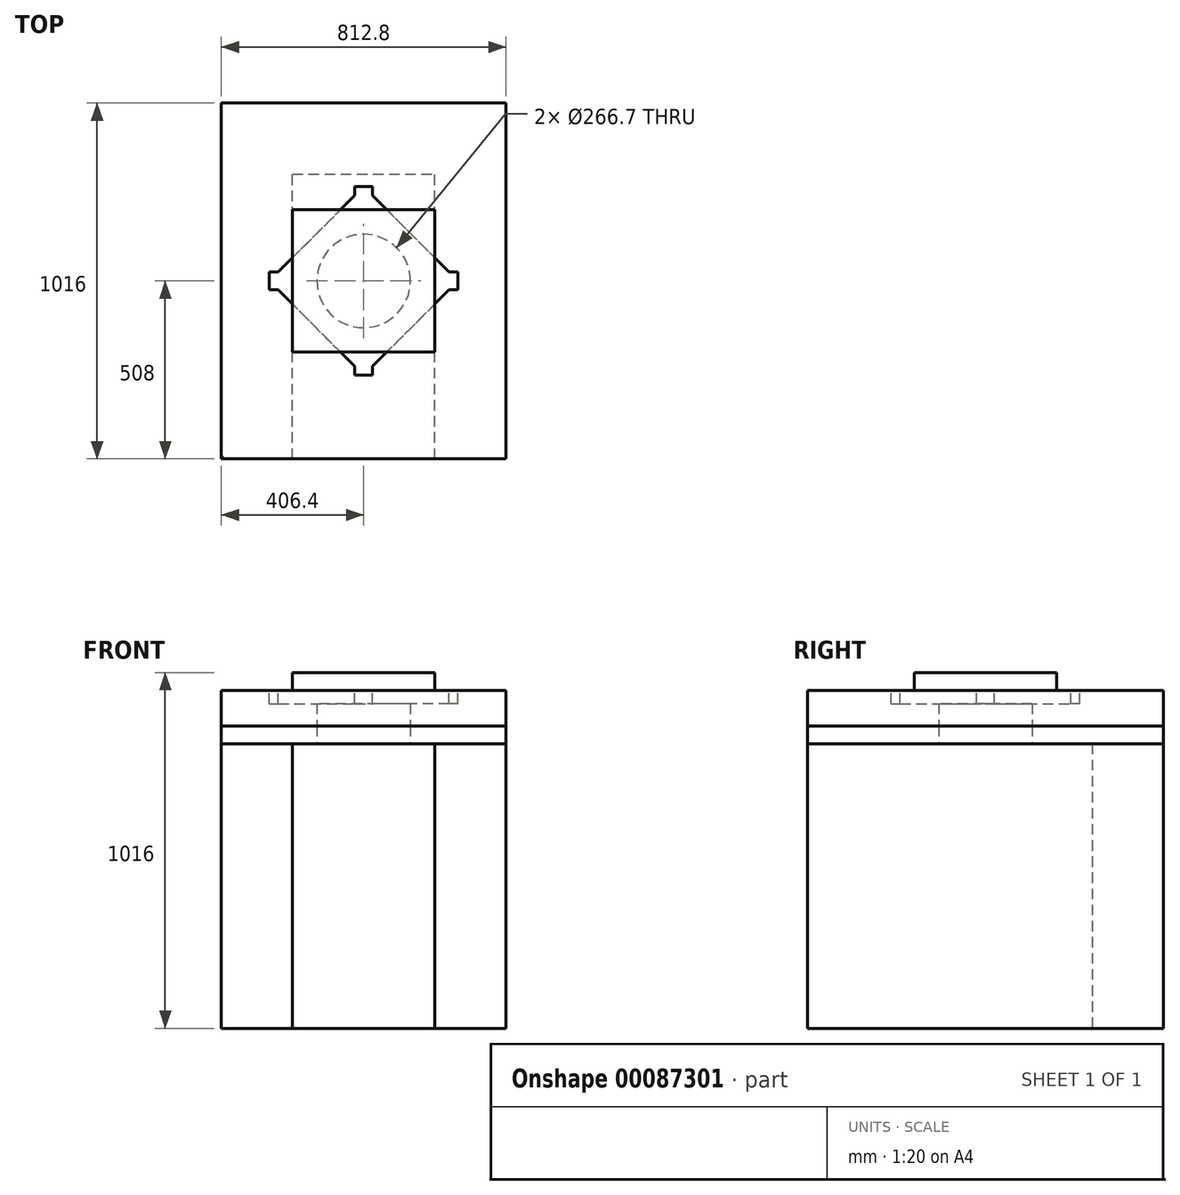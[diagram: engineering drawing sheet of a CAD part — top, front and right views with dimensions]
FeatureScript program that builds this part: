
annotation { "Feature Type Name" : "Feature", "Feature Type Description" : "" }
export const myFeature = defineFeature(function(context is Context, id is Id, definition is map)
    precondition{}
    {
        {
            var Q0;
            Q0=qCreatedBy(makeId("Top.planeOp"),FACE);
            var sketch = newSketch(context, id + "F0", { "sketchPlane" : qUnion([Q0])});
            skLineSegment(sketch, "E0.bottom", {"start": v(-406.4, 508) * mm, "end": v(0, 508) * mm});
            skLineSegment(sketch, "E0.top", {"start": v(-406.4, -508) * mm, "end": v(-203.2, -508) * mm});
            skLineSegment(sketch, "E0.left", {"start": v(-406.4, 508) * mm, "end": v(-406.4, 304.8) * mm});
            skLineSegment(sketch, "E0.right", {"start": v(406.4, 508) * mm, "end": v(406.4, 304.8) * mm});
            skPoint(sketch, "E0.middle", {"position": v(0, 0) * mm});
            skLineSegment(sketch, "E1.bottom", {"start": v(-203.2, -508) * mm, "end": v(-203.2, -508) * mm});
            skLineSegment(sketch, "E1.top", {"start": v(-203.2, 304.8) * mm, "end": v(203.2, 304.8) * mm});
            skLineSegment(sketch, "E1.left", {"start": v(-203.2, -508) * mm, "end": v(-203.2, -101.6) * mm});
            skLineSegment(sketch, "E1.right", {"start": v(203.2, -508) * mm, "end": v(203.2, -101.6) * mm});
            skLineSegment(sketch, "E2", {"start": v(-203.2, -508) * mm, "end": v(203.2, -508) * mm});
            skLineSegment(sketch, "E3", {"start": v(203.2, -508) * mm, "end": v(203.2, -508) * mm});
            skLineSegment(sketch, "E4", {"start": v(203.2, -508) * mm, "end": v(406.4, -508) * mm});
            skLineSegment(sketch, "E5", {"start": v(-406.4, -101.6) * mm, "end": v(-203.2, -101.6) * mm});
            skLineSegment(sketch, "E6", {"start": v(-406.4, 304.8) * mm, "end": v(-203.2, 304.8) * mm});
            skLineSegment(sketch, "E7", {"start": v(0, 304.8) * mm, "end": v(0, 508) * mm});
            skLineSegment(sketch, "E8", {"start": v(203.2, 304.8) * mm, "end": v(406.4, 304.8) * mm});
            skLineSegment(sketch, "E9", {"start": v(203.2, -101.6) * mm, "end": v(406.4, -101.6) * mm});
            skLineSegment(sketch, "E10", {"start": v(-406.4, 304.8) * mm, "end": v(-406.4, -101.6) * mm});
            skLineSegment(sketch, "E11", {"start": v(-406.4, -101.6) * mm, "end": v(-406.4, -508) * mm});
            skLineSegment(sketch, "E12", {"start": v(-203.2, -101.6) * mm, "end": v(-203.2, 304.8) * mm});
            skLineSegment(sketch, "E13", {"start": v(203.2, -101.6) * mm, "end": v(203.2, 304.8) * mm});
            skLineSegment(sketch, "E14", {"start": v(406.4, -101.6) * mm, "end": v(406.4, -508) * mm});
            skLineSegment(sketch, "E15", {"start": v(406.4, 304.8) * mm, "end": v(406.4, -101.6) * mm});
            skLineSegment(sketch, "E16", {"start": v(0, 508) * mm, "end": v(406.4, 508) * mm});
            skSolve(sketch);
        }
        {
            var Q0;
            Q0=makeQuery(id+"F0.imprint","IMPRINT",FACE,{"disambiguationData":[TD([[makeQuery(id+"F0.imprint","IMPRINT",EDGE,{"derivedFrom":sQuery(id+"F0.wireOp",EDGE,"E0.top")}),1.0]])]});
            var Q1;
            Q1=makeQuery(id+"F0.imprint","IMPRINT",FACE,{"disambiguationData":[TD([[makeQuery(id+"F0.imprint","IMPRINT",EDGE,{"derivedFrom":sQuery(id+"F0.wireOp",EDGE,"E5")}),1.0]])]});
            var Q2;
            Q2=makeQuery(id+"F0.imprint","IMPRINT",FACE,{"disambiguationData":[TD([[makeQuery(id+"F0.imprint","IMPRINT",EDGE,{"derivedFrom":sQuery(id+"F0.wireOp",EDGE,"E0.bottom")}),-1.0]])]});
            var Q3;
            Q3=makeQuery(id+"F0.imprint","IMPRINT",FACE,{"disambiguationData":[TD([[makeQuery(id+"F0.imprint","IMPRINT",EDGE,{"derivedFrom":sQuery(id+"F0.wireOp",EDGE,"E0.right")}),-1.0]])]});
            var Q4;
            Q4=makeQuery(id+"F0.imprint","IMPRINT",FACE,{"disambiguationData":[TD([[makeQuery(id+"F0.imprint","IMPRINT",EDGE,{"derivedFrom":sQuery(id+"F0.wireOp",EDGE,"E8")}),-1.0]])]});
            var Q5;
            Q5=makeQuery(id+"F0.imprint","IMPRINT",FACE,{"disambiguationData":[TD([[makeQuery(id+"F0.imprint","IMPRINT",EDGE,{"derivedFrom":sQuery(id+"F0.wireOp",EDGE,"E1.right")}),-1.0]])]});
            extrude(context, id + "F1", {"entities" : qUnion([Q0, Q1, Q2, Q3, Q4, Q5]), "depth" : 812.8 * mm});
        }
        {
            var Q0;
            Q0=makeQuery(id+"F1.opExtrude","CAP_FACE",FACE,{"disambiguationData":[OSD([sQuery(id+"F0.wireOp",EDGE,"E0.bottom"),sQuery(id+"F0.wireOp",EDGE,"E0.top"),sQuery(id+"F0.wireOp",EDGE,"E0.left"),sQuery(id+"F0.wireOp",EDGE,"E0.right"),sQuery(id+"F0.wireOp",EDGE,"E1.top"),sQuery(id+"F0.wireOp",EDGE,"E1.left"),sQuery(id+"F0.wireOp",EDGE,"E1.right"),sQuery(id+"F0.wireOp",EDGE,"E4"),sQuery(id+"F0.wireOp",EDGE,"E10"),sQuery(id+"F0.wireOp",EDGE,"E11"),sQuery(id+"F0.wireOp",EDGE,"E12"),sQuery(id+"F0.wireOp",EDGE,"E13"),sQuery(id+"F0.wireOp",EDGE,"E14"),sQuery(id+"F0.wireOp",EDGE,"E15"),sQuery(id+"F0.wireOp",EDGE,"E16")])],"isStart":false});
            var sketch = newSketch(context, id + "F2", { "sketchPlane" : qUnion([Q0])});
            skPoint(sketch, "E17.0", {"position": v(-406.4, 508) * mm});
            skPoint(sketch, "E17.1", {"position": v(406.4, 508) * mm});
            skPoint(sketch, "E17.2", {"position": v(406.4, -508) * mm});
            skPoint(sketch, "E17.3", {"position": v(-406.4, -508) * mm});
            skLineSegment(sketch, "E18.bottom", {"start": v(-406.4, 508) * mm, "end": v(406.4, 508) * mm});
            skLineSegment(sketch, "E18.top", {"start": v(-406.4, -508) * mm, "end": v(406.4, -508) * mm});
            skLineSegment(sketch, "E18.left", {"start": v(-406.4, 508) * mm, "end": v(-406.4, -508) * mm});
            skLineSegment(sketch, "E18.right", {"start": v(406.4, 508) * mm, "end": v(406.4, -508) * mm});
            skCircle(sketch, "E19", {"center": v(0, 0) * mm, "radius": 133.35 * mm});
            skSolve(sketch);
        }
        {
            var Q0;
            Q0=makeQuery(id+"F2.imprint","IMPRINT",FACE,{"disambiguationData":[TD([[makeQuery(id+"F2.imprint","IMPRINT",EDGE,{"derivedFrom":sQuery(id+"F2.wireOp",EDGE,"E18.bottom")}),-1.0]])]});
            var Q1;
            Q1=makeQuery(id+"F2.imprint","IMPRINT",FACE,{"disambiguationData":[TD([[makeQuery(id+"F2.imprint","IMPRINT",EDGE,{"derivedFrom":sQuery(id+"F2.wireOp",EDGE,"E19")}),-1.0]])]});
            extrude(context, id + "F3", {"entities" : qUnion([Q0, Q1]), "depth" : 50.8 * mm});
        }
        {
            var Q0;
            Q0=makeQuery(id+"F3.opExtrude","CAP_FACE",FACE,{"disambiguationData":[OSD([sQuery(id+"F2.wireOp",EDGE,"E18.bottom"),sQuery(id+"F2.wireOp",EDGE,"E18.top"),sQuery(id+"F2.wireOp",EDGE,"E18.left"),sQuery(id+"F2.wireOp",EDGE,"E18.right"),sQuery(id+"F2.wireOp",EDGE,"E19")])],"isStart":false});
            var sketch = newSketch(context, id + "F4", { "sketchPlane" : qUnion([Q0])});
            skCircle(sketch, "E20.4", {"center": v(0, 0) * mm, "radius": 133.35 * mm});
            skLineSegment(sketch, "E21.0", {"start": v(-406.4, 508) * mm, "end": v(-406.4, -508) * mm});
            skLineSegment(sketch, "E21.1", {"start": v(-406.4, 508) * mm, "end": v(406.4, 508) * mm});
            skLineSegment(sketch, "E21.2", {"start": v(406.4, 508) * mm, "end": v(406.4, -508) * mm});
            skLineSegment(sketch, "E21.3", {"start": v(-406.4, -508) * mm, "end": v(406.4, -508) * mm});
            skSolve(sketch);
        }
        {
            var Q0;
            Q0=makeQuery(id+"F4.imprint","IMPRINT",FACE,{"disambiguationData":[TD([[makeQuery(id+"F4.imprint","IMPRINT",EDGE,{"derivedFrom":sQuery(id+"F4.wireOp",EDGE,"E20.4")}),-1.0]])]});
            extrude(context, id + "F5", {"entities" : qUnion([Q0]), "depth" : 101.6 * mm});
        }
        {
            var Q0;
            Q0=makeQuery(id+"F5.opExtrude","CAP_FACE",FACE,{"disambiguationData":[OSD([sQuery(id+"F4.wireOp",EDGE,"E20.4"),sQuery(id+"F4.wireOp",EDGE,"E21.0"),sQuery(id+"F4.wireOp",EDGE,"E21.1"),sQuery(id+"F4.wireOp",EDGE,"E21.2"),sQuery(id+"F4.wireOp",EDGE,"E21.3")])],"isStart":false});
            var sketch = newSketch(context, id + "F6", { "sketchPlane" : qUnion([Q0])});
            skPoint(sketch, "E22.0", {"position": v(0, 0) * mm});
            skLineSegment(sketch, "E23", {"start": v(-203.2, 203.2) * mm, "end": v(203.2, 203.2) * mm});
            skLineSegment(sketch, "E24", {"start": v(203.2, 203.2) * mm, "end": v(203.2, -203.2) * mm});
            skLineSegment(sketch, "E25", {"start": v(203.2, -203.2) * mm, "end": v(-203.2, -203.2) * mm});
            skLineSegment(sketch, "E26", {"start": v(-203.2, -203.2) * mm, "end": v(-203.2, 203.2) * mm});
            skLineSegment(sketch, "E27", {"start": v(0, 203.2) * mm, "end": v(0, -203.2) * mm, "construction": true});
            skLineSegment(sketch, "E28", {"start": v(203.2, 0) * mm, "end": v(0, 0) * mm, "construction": true});
            skLineSegment(sketch, "E29", {"start": v(0, 0) * mm, "end": v(-203.2, 0) * mm, "construction": true});
            skSolve(sketch);
        }
        {
            var Q0;
            Q0=makeQuery(id+"F6.imprint","IMPRINT",FACE,{"disambiguationData":[TD([[makeQuery(id+"F6.imprint","IMPRINT",EDGE,{"derivedFrom":makeQuery(id+"F5.opExtrude","CAP_EDGE",EDGE,{"disambiguationData":[OSD([sQuery(id+"F4.wireOp",EDGE,"E20.4")])],"isStart":false})}),1.0]])]});
            var Q1;
            Q1=makeQuery(id+"F6.imprint","IMPRINT",FACE,{"disambiguationData":[TD([[makeQuery(id+"F6.imprint","IMPRINT",EDGE,{"derivedFrom":sQuery(id+"F6.wireOp",EDGE,"E23")}),-1.0]])]});
            extrude(context, id + "F7", {"entities" : qUnion([Q0, Q1]), "depth" : 50.8 * mm});
        }
        {
            var Q0;
            Q0=makeQuery(id+"F5.opExtrude","CAP_FACE",FACE,{"disambiguationData":[OSD([sQuery(id+"F4.wireOp",EDGE,"E20.4"),sQuery(id+"F4.wireOp",EDGE,"E21.0"),sQuery(id+"F4.wireOp",EDGE,"E21.1"),sQuery(id+"F4.wireOp",EDGE,"E21.2"),sQuery(id+"F4.wireOp",EDGE,"E21.3")])],"isStart":false});
            var sketch = newSketch(context, id + "F8", { "sketchPlane" : qUnion([Q0])});
            skPoint(sketch, "E30.0", {"position": v(0, 0) * mm});
            skLineSegment(sketch, "E31", {"start": v(0, 269.4) * mm, "end": v(269.4, 0) * mm});
            skLineSegment(sketch, "E32", {"start": v(269.4, 0) * mm, "end": v(0, -269.4) * mm});
            skLineSegment(sketch, "E33", {"start": v(0, -269.4) * mm, "end": v(-269.4, 0) * mm});
            skLineSegment(sketch, "E34", {"start": v(-269.4, 0) * mm, "end": v(0, 269.4) * mm});
            skLineSegment(sketch, "E35", {"start": v(-25.4, 269.4) * mm, "end": v(25.4, 269.4) * mm});
            skLineSegment(sketch, "E36", {"start": v(25.4, 269.4) * mm, "end": v(25.4, 244) * mm});
            skLineSegment(sketch, "E37", {"start": v(-25.4, 269.4) * mm, "end": v(-25.4, 244) * mm});
            skLineSegment(sketch, "E38", {"start": v(269.4, 25.4) * mm, "end": v(269.4, -25.4) * mm});
            skLineSegment(sketch, "E39", {"start": v(269.4, 25.4) * mm, "end": v(244, 25.4) * mm});
            skLineSegment(sketch, "E40", {"start": v(269.4, -25.4) * mm, "end": v(244, -25.4) * mm});
            skLineSegment(sketch, "E41", {"start": v(25.4, -269.4) * mm, "end": v(-25.4, -269.4) * mm});
            skLineSegment(sketch, "E42", {"start": v(-25.4, -269.4) * mm, "end": v(-25.4, -244) * mm});
            skLineSegment(sketch, "E43", {"start": v(25.4, -269.4) * mm, "end": v(25.4, -244) * mm});
            skLineSegment(sketch, "E44", {"start": v(-269.4, 25.4) * mm, "end": v(-269.4, -25.4) * mm});
            skLineSegment(sketch, "E45", {"start": v(-269.4, -25.4) * mm, "end": v(-244, -25.4) * mm});
            skLineSegment(sketch, "E46", {"start": v(-269.4, 25.4) * mm, "end": v(-244, 25.4) * mm});
            skSolve(sketch);
        }
        {
            var Q0;
            Q0 = qSketchRegion(id + "F8", true);
            extrude(context, id + "F9", {"entities" : qUnion([Q0]), "operationType" : NewBodyOperationType.REMOVE, "oppositeDirection" : true, "depth" : 38.1 * mm});
        }
        {
            var Q0;
            Q0=makeQuery(id+"F3.opExtrude","SWEPT_EDGE",EDGE,{"disambiguationData":[OSD([sQuery(id+"F2.wireOp",EDGE,"E18.top"),sQuery(id+"F2.wireOp",EDGE,"E18.left")])]});
            fillet(context, id + "F10", {"entities" : qUnion([Q0]), "radius" : 12.7 * mm, "tangentPropagation" : true, "allowEdgeOverflow" : false});
        }
        {
            var Q0;
            Q0=makeQuery(id+"F5.opExtrude","SWEPT_EDGE",EDGE,{"disambiguationData":[OSD([sQuery(id+"F4.wireOp",EDGE,"E21.0"),sQuery(id+"F4.wireOp",EDGE,"E21.3")])]});
            fillet(context, id + "F11", {"entities" : qUnion([Q0]), "radius" : 12.7 * mm, "tangentPropagation" : true, "allowEdgeOverflow" : false});
        }
    });
